# Revit family: Electronics_Amplifier_Biamp_Tesira_4-Channel_AMP-A460H__
name_source: partatom
category: Communication Devices
units: mm (PartAtom-declared; Revit-internal decimal feet)

## family parameters
Cut with Voids When Loaded = Yes
Host = Face
Maintain Annotation Orientation = No
OmniClass Number = 23.85.10.11.14.14.17
OmniClass Title = Sound Amplifiers
Part Type = Normal
Room Calculation Point = No
Round Connector Dimension = Use Diameter
Shared = No

## types (1)
- AMP-A460H
    Amplifier Topology = Class D
    Apparent Load = 144 VA
    Bridged = 4 ohm, 8 ohm: 120W; 70V/100V: 120W
    Compliance = UL and C-UL listed (USA and Canada) FCC Part 15B (USA) CE Marked (Europe) RCM (Australia) EAC (Eurasian Customs Union) RoHS Directive (Europe) CCC (China)KCC (Korea)
    Connector Description = 100-240VAC, 50/60Hz
    Cooling = Convection
    Current = 1 A
    Default Elevation = 48 "
    Depth = 10.5 "
    Description = Tesira® AMP-A460H 4-Channel, 60W Amplifier
    Dynamic Range = 100 dB
    Frequency Response = ± 1 dB
    Height = 1.7 "
    Housing Material = Biamp - Metal - Silver
    Humidity = 0-95% relative humidity (non-condensing)
    Indicators Rear Panel = 80Hz HPF (on/off) Mode selection (standard/bridged) Constant Voltage selection (bridged mode only)
    Input Sensitivity = 8 ohm, 70V: 0 dBu; 100V: +1.6 dBu
    Manufacturer = Biamp
    Model = AMP-A460H
    Number of Channels = 4
    Number of Poles = 1
    Power Factor = 1
    Product Documentation Link = https://downloads.biamp.com
    Product Page URL = https://www.biamp.com
    Product data url = https://www.bimobject.com
    Single Channel = 4 ohm, 8 ohm: 60W
    THD+N = 20Hz - 20kHz, at rated power: <0.3%
    Temperature Range = 32 - 104° F (0 - 40° C)
    URL = https://www.biamp.com
    Voltage = 120 V
    Weight = 4.20 lbf
    Width = 8.7 "

## geometry (parser evidence)
native form markers: Sweep x4
no freeform markers — native parametric forms only
